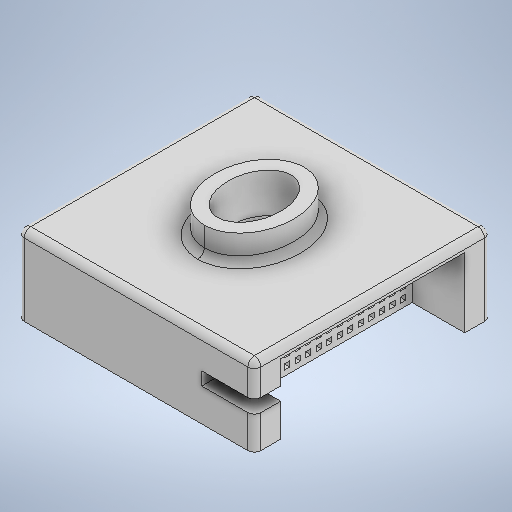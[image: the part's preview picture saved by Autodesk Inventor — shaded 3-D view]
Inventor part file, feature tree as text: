
AUTODESK INVENTOR PART (.ipt)
format: ipt  version: 2025.2 (Build 292293000, 293)  size: 908,800 bytes
history: native  units: in
note: dims shown in document units (in); Inventor stores cm internally (conversion verified against a paired STEP export)
features: sketch x11, extrude x10, fillet x3, shell x1, pattern_linear x1, projected_geometry x1
ambient origin geometry x8: Origin, YZ Plane, XZ Plane, XY Plane, X Axis, Y Axis, Z Axis, Center Point
bodies: Solid1 (feature_tree)
feature tree (27):
  extrude  "Extrusion1"  Depth=9.0in
  fillet  "Fillet1"  Radius=3.0in
  sketch  "Sketch2"  dims[d8=0.25in d9=0.5in]
  extrude  "Extrusion2"  Depth=0.25in
  shell  "Shell2"  Thickness=2.3in
  extrude  "Extrusion3"  Depth=0.25in
  extrude  "Extrusion4"  Depth=0.5in
  extrude  "Extrusion5"  Depth=1.4in
  extrude  "Extrusion6"  Depth=0.25in
  fillet  "Fillet4"  Radius=1.0in
  extrude  "Extrusion7"  Depth=0.25in TaperAngle=0.0deg
  fillet  "Fillet5"  Radius=0.25in
  extrude  "Extrusion8"  Depth=0.25in
  extrude  "Extrusion9"  Depth=3.5in
  pattern_linear  "Rectangular Pattern2"  Spacing1=0.25in  [1 undecoded]
  extrude  "Extrusion10"  Depth=0.2in
  sketch  "Sketch1"  dims[d0=9.0in d1=9.0in d2=3.0in d3=0.0in]
  sketch  "Sketch3"  dims[d10=2.0in d11=0.0in d12=0.5in]
  sketch  "Sketch4"  dims[d13=1.0in d14=1.4in]
  sketch  "Sketch5"  dims[d15=2.0in d16=0.0in d19=0.25in d20=1.0in d21=0.0in]
  sketch  "Sketch6"  dims[d22=0.5in d23=1.0in d24=0.0in d25=0.25in]
  sketch  "Sketch7"  dims[d26=1.0in d27=0.0in d28=0.25in]
  sketch  "Sketch8"  dims[d29=7.0in d30=3.5in]
  projected_geometry  "Projected Loop1"
  sketch  "Sketch Rectangular Pattern1"  dims[d4=0.25in d6=7.0in d7=2.3in]
  sketch  "Sketch10"  dims[d31=7.0in]
  sketch  "Sketch11"  dims[d32=0.125in d33=0.0in d34=0.25in d36=0.2in d37=0.2in d38=6.6929in d40=0.4in d41=1.9685in d43=0.4in d46=0.5in d47=0.0in d55=2.0in d56=0.0in d58=6.6929in d60=0.4in d61=2.3622in d63=0.4in d64=0.8in d65=0.0in d35=0.0344in d57=0.5in]
note: 1 required parameter value undecoded (feature->parameter linkage not recoverable at this tier; creation-order binding heuristic only, values carry confidence <= 0.55)
